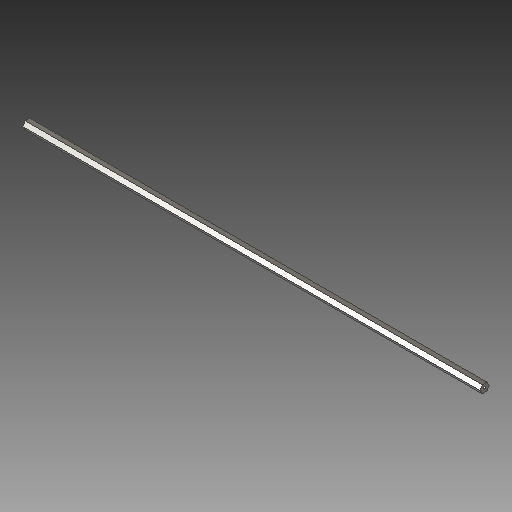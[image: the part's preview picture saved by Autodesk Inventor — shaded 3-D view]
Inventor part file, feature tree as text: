
AUTODESK INVENTOR PART (.ipt)
format: ipt  version: 2017 SP1 (Build 210196100, 196)  size: 100,864 bytes
history: native  units: in
note: dims shown in document units (in); Inventor stores cm internally (conversion verified against a paired STEP export)
features: extrude x1, sketch x1
ambient origin geometry x8: Origin, YZ Plane, XZ Plane, XY Plane, X Axis, Y Axis, Z Axis, Center Point
bodies: Solid1 (feature_tree)
feature tree (2):
  extrude  "Extrusion1"  Depth=0.375in
  sketch  "Sketch1"  dims[d1=21.75in d2=0.0in d3=0.375in d4=0.1in]
